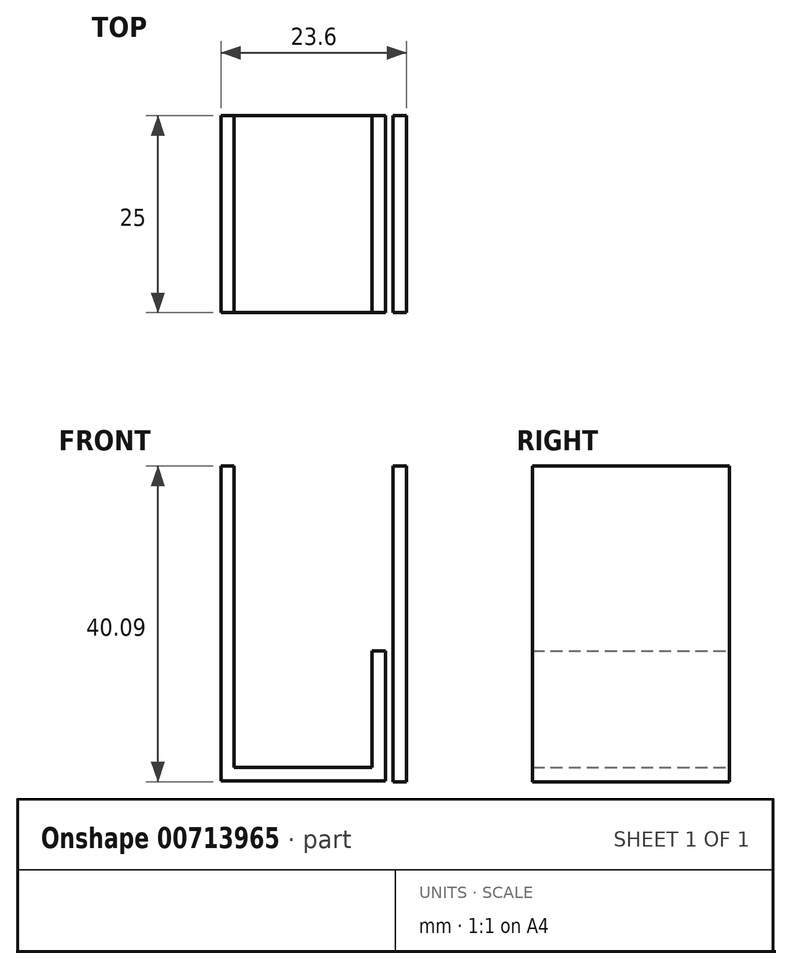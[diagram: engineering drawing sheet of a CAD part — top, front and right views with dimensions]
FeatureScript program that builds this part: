
annotation { "Feature Type Name" : "Feature", "Feature Type Description" : "" }
export const myFeature = defineFeature(function(context is Context, id is Id, definition is map)
    precondition{}
    {
        {
            var Q0;
            Q0=qCreatedBy(makeId("Front.planeOp"),FACE);
            var sketch = newSketch(context, id + "F0", { "sketchPlane" : qUnion([Q0])});
            skLineSegment(sketch, "E0", {"start": v(0, 0) * mm, "end": v(17.5, 0) * mm});
            skLineSegment(sketch, "E1", {"start": v(17.5, 0) * mm, "end": v(17.5, 14.8) * mm});
            skLineSegment(sketch, "E2", {"start": v(17.5, 14.8) * mm, "end": v(19.2, 14.8) * mm});
            skLineSegment(sketch, "E3", {"start": v(19.2, 14.8) * mm, "end": v(19.2, -1.7) * mm});
            skLineSegment(sketch, "E4", {"start": v(19.2, -1.7) * mm, "end": v(-1.7, -1.7) * mm});
            skLineSegment(sketch, "E5", {"start": v(-1.7, -1.7) * mm, "end": v(-1.7, 38.3) * mm});
            skLineSegment(sketch, "E6", {"start": v(-1.7, 38.3) * mm, "end": v(0, 38.3) * mm});
            skLineSegment(sketch, "E7", {"start": v(0, 38.3) * mm, "end": v(0, 0) * mm});
            skLineSegment(sketch, "E8.bottom", {"start": v(20.2, 38.3) * mm, "end": v(21.9, 38.3) * mm});
            skLineSegment(sketch, "E8.top", {"start": v(20.2, -1.79) * mm, "end": v(21.9, -1.79) * mm});
            skLineSegment(sketch, "E8.left", {"start": v(20.2, 38.3) * mm, "end": v(20.2, -1.79) * mm});
            skLineSegment(sketch, "E8.right", {"start": v(21.9, 38.3) * mm, "end": v(21.9, -1.79) * mm});
            skSolve(sketch);
        }
        {
            var Q0;
            Q0=makeQuery(id+"F0.imprint","IMPRINT",FACE,{"disambiguationData":[TD([[makeQuery(id+"F0.imprint","IMPRINT",EDGE,{"derivedFrom":sQuery(id+"F0.wireOp",EDGE,"E0")}),-1.0]])]});
            var Q1;
            Q1=makeQuery(id+"F0.imprint","IMPRINT",FACE,{"disambiguationData":[TD([[makeQuery(id+"F0.imprint","IMPRINT",EDGE,{"derivedFrom":sQuery(id+"F0.wireOp",EDGE,"E8.bottom")}),-1.0]])]});
            extrude(context, id + "F1", {"entities" : qUnion([Q0, Q1]), "endBound" : BoundingType.SYMMETRIC, "depth" : 25 * mm, "offsetDistance" : 25 * mm});
        }
        {
            var Q0;
            Q0=makeQuery(id+"F1.opExtrude","SWEPT_FACE",FACE,{"disambiguationData":[OSD([sQuery(id+"F0.wireOp",EDGE,"E8.left")])]});
            var sketch = newSketch(context, id + "F2", { "sketchPlane" : qUnion([Q0])});
            skPoint(sketch, "E9", {"position": v(0, 23.21) * mm});
            skSolve(sketch);
        }
    });
